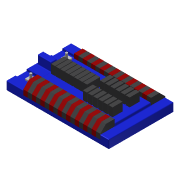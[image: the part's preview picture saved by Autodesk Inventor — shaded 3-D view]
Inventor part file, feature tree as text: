
AUTODESK INVENTOR PART (.ipt)
format: ipt  version: 2013 (Build 170138000, 138)  size: 646,656 bytes
history: native  units: in
note: dims shown in document units (in); Inventor stores cm internally (conversion verified against a paired STEP export)
features: extrude x11, sketch x11, projected_geometry x6, pattern_linear x5, other x1, fillet x1, chamfer x1, move_body x1
ambient origin geometry x8: Origin, YZ Plane, XZ Plane, XY Plane, X Axis, Y Axis, Z Axis, Center Point
bodies: Solid4 (feature_tree), Solid5 (feature_tree), Solid6 (feature_tree), Solid7 (feature_tree), Solid8 (feature_tree)
feature tree (37):
  other  "Blue"
  extrude  "Extrusion1"  Depth=5.7in
  extrude  "Extrusion4"  Depth=0.75in
  extrude  "Extrusion5"  Depth=0.375in
  pattern_linear  "Rectangular Pattern2"  Count1=9 Spacing1=0.75in
  pattern_linear  "Rectangular Pattern3"  Count1=9 Spacing1=0.75in
  extrude  "Extrusion6"  Depth=0.205in TaperAngle=0.0deg
  extrude  "Extrusion7"  Depth=0.0625in
  extrude  "Extrusion8"  Depth=1.15in
  fillet  "Fillet1"  Radius=0.35in
  chamfer  "Chamfer1"  Distance=0.75in
  extrude  "Extrusion9"  Depth=3.1496in
  pattern_linear  "Rectangular Pattern4"  Spacing1=0.35in  [1 undecoded]
  extrude  "Extrusion10"  Depth=0.875in
  pattern_linear  "Rectangular Pattern5"  Spacing1=0.25in  [1 undecoded]
  extrude  "Extrusion11"  Depth=0.35in
  extrude  "Extrusion12"  Depth=0.875in
  extrude  "Extrusion13"  Depth=0.625in
  pattern_linear  "Rectangular Pattern6"  Spacing1=0.75in  [1 undecoded]
  move_body  "Move Body1"
  sketch  "Sketch2"  dims[d0=9.0in d2=5.7in]
  sketch  "Sketch3"  dims[d3=0.38in d4=0.0in d5=0.75in]
  sketch  "Sketch5"  dims[d6=1.25in d14=0.375in]
  projected_geometry  "Projected Loop3"
  projected_geometry  "Projected Loop4"
  sketch  "Sketch6"  dims[d17=0.95in d18=0.0in]
  projected_geometry  "Projected Loop5"
  projected_geometry  "Projected Loop6"
  projected_geometry  "Projected Loop7"
  projected_geometry  "Projected Loop8"
  sketch  "Sketch7"  dims[d19=0.375in]
  sketch  "Sketch8"  dims[d20=0.375in]
  sketch  "Sketch9"  dims[d21=0.95in d22=0.0in d23=3.5433in d25=0.75in d26=3.5433in d28=0.75in]
  sketch  "Sketch10"  dims[d29=0.375in d30=0.0026in d31=0.205in d32=0.0in]
  sketch  "Sketch11"  dims[d33=0.75in d34=0.0in d35=0.0625in]
  sketch  "Sketch12"  dims[d36=0.5in d37=0.125in d38=45.0deg d39=1.15in d41=0.35in d42=0.75in d43=0.0in]
  sketch  "Sketch13"  dims[d44=0.1in d45=3.1496in d47=0.4in d48=0.35in d49=0.875in d50=0.25in d51=0.35in d52=0.875in d53=0.625in d54=0.75in d55=0.0in d56=2.3622in d58=0.45in d59=1.0in d61=0.125in d62=2.0in d63=0.75in d64=0.75in d65=0.25in d66=0.18in d67=0.0in d68=0.512in d70=0.512in d71=0.625in d72=0.125in d73=0.0in d74=0.1969in d75=0.4in d76=0.0in d77=0.7874in d79=3.131in d80=0.0in d81=0.0in d82=-2.85in]
note: 3 required parameter values undecoded (feature->parameter linkage not recoverable at this tier; creation-order binding heuristic only, values carry confidence <= 0.55)
